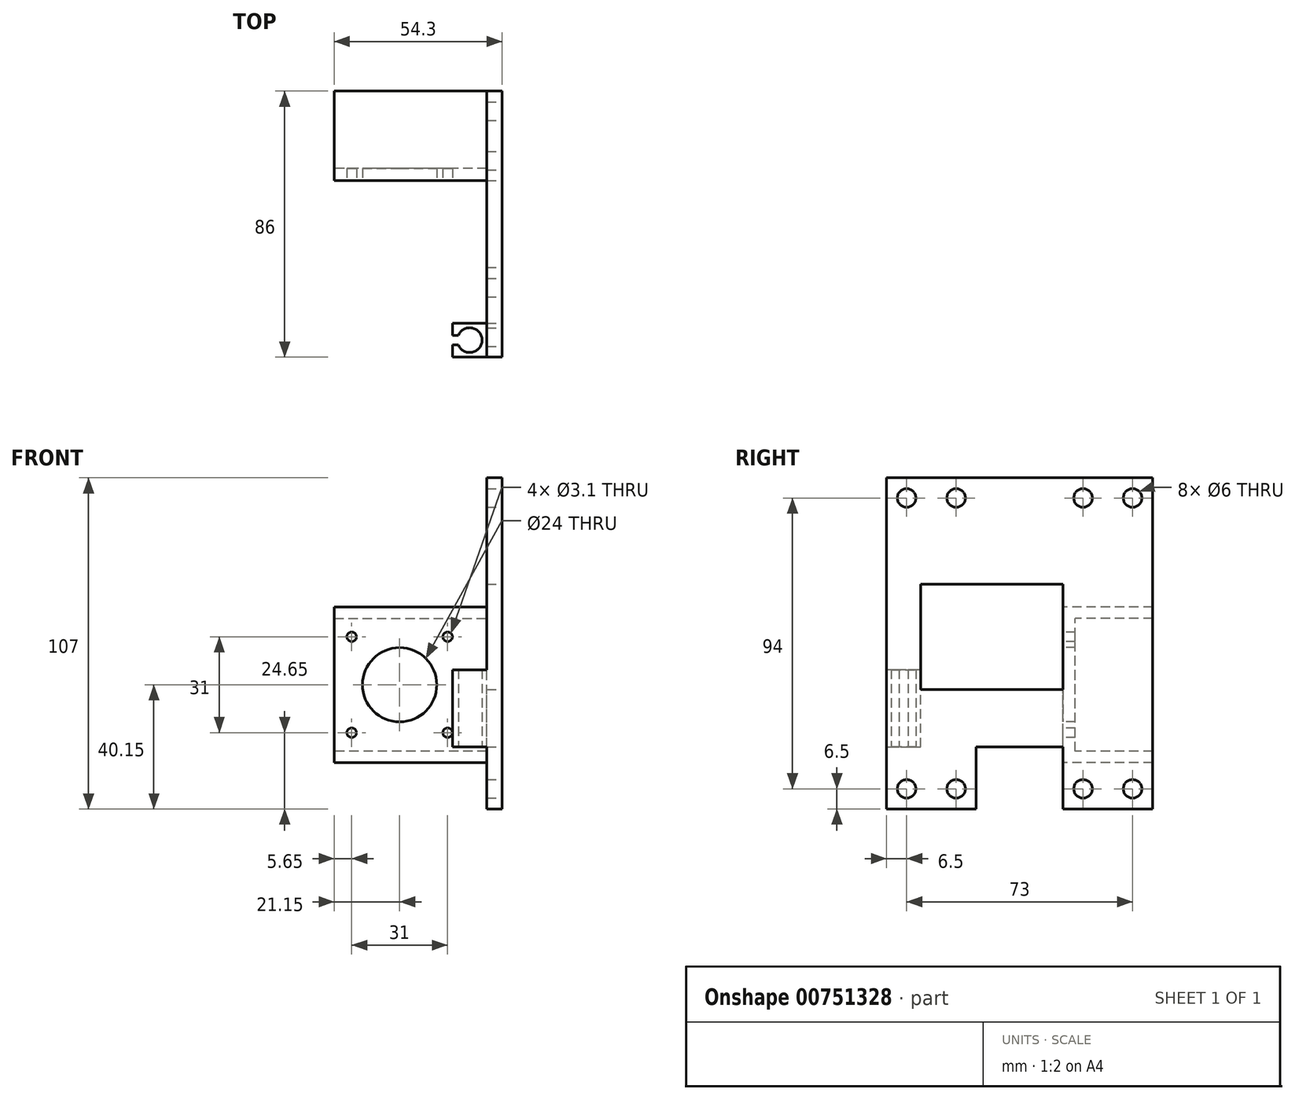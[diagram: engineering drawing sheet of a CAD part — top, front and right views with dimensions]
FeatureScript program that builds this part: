
annotation { "Feature Type Name" : "Feature", "Feature Type Description" : "" }
export const myFeature = defineFeature(function(context is Context, id is Id, definition is map)
    precondition{}
    {
        {
            var Q0;
            Q0=qCreatedBy(makeId("Front.planeOp"),FACE);
            var sketch = newSketch(context, id + "F0", { "sketchPlane" : qUnion([Q0])});
            skCircle(sketch, "E0", {"center": v(0, 0) * mm, "radius": 11 * mm, "construction": true});
            skLineSegment(sketch, "E1.bottom", {"start": v(15.5, 15.5) * mm, "end": v(-15.5, 15.5) * mm, "construction": true});
            skLineSegment(sketch, "E1.top", {"start": v(15.5, -15.5) * mm, "end": v(-15.5, -15.5) * mm, "construction": true});
            skLineSegment(sketch, "E1.left", {"start": v(15.5, 15.5) * mm, "end": v(15.5, -15.5) * mm, "construction": true});
            skLineSegment(sketch, "E1.right", {"start": v(-15.5, 15.5) * mm, "end": v(-15.5, -15.5) * mm, "construction": true});
            skCircle(sketch, "E2", {"center": v(15.5, 15.5) * mm, "radius": 1.5 * mm, "construction": true});
            skCircle(sketch, "E3", {"center": v(-15.5, 15.5) * mm, "radius": 1.5 * mm, "construction": true});
            skCircle(sketch, "E4", {"center": v(-15.5, -15.5) * mm, "radius": 1.5 * mm, "construction": true});
            skCircle(sketch, "E5", {"center": v(15.5, -15.5) * mm, "radius": 1.5 * mm, "construction": true});
            skCircle(sketch, "E6", {"center": v(15.5, 15.5) * mm, "radius": 17 * mm, "construction": true});
            skLineSegment(sketch, "E7.bottom", {"start": v(21.15, 21.15) * mm, "end": v(-21.15, 21.15) * mm, "construction": true});
            skLineSegment(sketch, "E7.top", {"start": v(21.15, -21.15) * mm, "end": v(-21.15, -21.15) * mm, "construction": true});
            skLineSegment(sketch, "E7.left", {"start": v(21.15, 21.15) * mm, "end": v(21.15, -21.15) * mm, "construction": true});
            skLineSegment(sketch, "E7.right", {"start": v(-21.15, 21.15) * mm, "end": v(-21.15, -21.15) * mm, "construction": true});
            skLineSegment(sketch, "E8", {"start": v(-43.83, -21) * mm, "end": v(88.96, -21) * mm, "construction": true});
            skSolve(sketch);
        }
        {
            var Q0;
            Q0=qCreatedBy(makeId("Top.planeOp"),FACE);
            var sketch = newSketch(context, id + "F1", { "sketchPlane" : qUnion([Q0])});
            skLineSegment(sketch, "E9.bottom", {"start": v(0, 0) * mm, "end": v(10.6, 0) * mm, "construction": true});
            skLineSegment(sketch, "E9.top", {"start": v(0, -13.5) * mm, "end": v(10.6, -13.5) * mm, "construction": true});
            skLineSegment(sketch, "E9.left", {"start": v(0, 0) * mm, "end": v(0, -13.5) * mm, "construction": true});
            skLineSegment(sketch, "E9.right", {"start": v(10.6, 0) * mm, "end": v(10.6, -13.5) * mm, "construction": true});
            skLineSegment(sketch, "E10", {"start": v(18.9, 0) * mm, "end": v(23.9, 0) * mm});
            skPoint(sketch, "E11", {"position": v(21.4, 0) * mm});
            skCircle(sketch, "E12", {"center": v(10.6, -13.5) * mm, "radius": 4 * mm, "construction": true});
            skLineSegment(sketch, "E13", {"start": v(10.6, -13.5) * mm, "end": v(10.6, -36.5) * mm, "construction": true});
            skLineSegment(sketch, "E14", {"start": v(10.6, -36.5) * mm, "end": v(19.6, -36.5) * mm, "construction": true});
            skCircle(sketch, "E15", {"center": v(19.6, -36.5) * mm, "radius": 4 * mm, "construction": true});
            skSolve(sketch);
        }
        {
            var Q0;
            Q0=qCreatedBy(makeId("Front.planeOp"),FACE);
            var sketch = newSketch(context, id + "F2", { "sketchPlane" : qUnion([Q0])});
            skLineSegment(sketch, "E16.0", {"start": v(33.15, 60.35) * mm, "end": v(33.15, -33.65) * mm});
            skLineSegment(sketch, "E17", {"start": v(33.15, 60.35) * mm, "end": v(33.15, 66.85) * mm});
            skLineSegment(sketch, "E18", {"start": v(33.15, -33.65) * mm, "end": v(33.15, -40.15) * mm});
            skLineSegment(sketch, "E19.0", {"start": v(29.15, -25.15) * mm, "end": v(-21.15, -25.15) * mm});
            skLineSegment(sketch, "E20", {"start": v(29.15, -25.15) * mm, "end": v(29.15, -40.15) * mm});
            skLineSegment(sketch, "E21", {"start": v(29.15, -40.15) * mm, "end": v(33.15, -40.15) * mm});
            skLineSegment(sketch, "E22.0", {"start": v(21.45, -21.45) * mm, "end": v(-21.15, -21.45) * mm});
            skLineSegment(sketch, "E22.1", {"start": v(21.45, 66.85) * mm, "end": v(21.45, -21.45) * mm, "construction": true});
            skLineSegment(sketch, "E23", {"start": v(-21.15, -21.45) * mm, "end": v(-21.15, -25.15) * mm});
            skLineSegment(sketch, "E24", {"start": v(21.45, 66.85) * mm, "end": v(33.15, 66.85) * mm});
            skPoint(sketch, "E25.0", {"position": v(-21.15, 21.15) * mm});
            skLineSegment(sketch, "E26", {"start": v(-21.15, 21.15) * mm, "end": v(21.45, 21.15) * mm, "construction": true});
            skLineSegment(sketch, "E27", {"start": v(-21.15, 21.15) * mm, "end": v(-21.15, -21.45) * mm});
            skCircle(sketch, "E28.0", {"center": v(0, 0) * mm, "radius": 12 * mm});
            skCircle(sketch, "E29.0", {"center": v(15.5, 15.5) * mm, "radius": 1.55 * mm});
            skCircle(sketch, "E30.0", {"center": v(-15.5, 15.5) * mm, "radius": 1.55 * mm});
            skCircle(sketch, "E31.0", {"center": v(-15.5, -15.5) * mm, "radius": 1.55 * mm});
            skCircle(sketch, "E32.0", {"center": v(15.5, -15.5) * mm, "radius": 1.55 * mm});
            skLineSegment(sketch, "E33", {"start": v(29.15, -21.45) * mm, "end": v(29.15, 66.85) * mm});
            skLineSegment(sketch, "E34", {"start": v(21.45, -21.45) * mm, "end": v(29.15, -21.45) * mm});
            skLineSegment(sketch, "E35", {"start": v(21.45, 21.15) * mm, "end": v(29.15, 21.15) * mm, "construction": true});
            skLineSegment(sketch, "E36", {"start": v(29.15, -21.45) * mm, "end": v(29.15, -25.15) * mm});
            skLineSegment(sketch, "E37.0", {"start": v(-21.15, 21.45) * mm, "end": v(29.15, 21.45) * mm});
            skLineSegment(sketch, "E38", {"start": v(-21.15, 21.15) * mm, "end": v(-21.15, 25.15) * mm});
            skLineSegment(sketch, "E39", {"start": v(-21.15, 25.15) * mm, "end": v(29.15, 25.15) * mm});
            skSolve(sketch);
        }
        {
            var Q0;
            Q0=qCreatedBy(makeId("Right.planeOp"),FACE);
            var sketch = newSketch(context, id + "F3", { "sketchPlane" : qUnion([Q0])});
            skPoint(sketch, "E40.0", {"position": v(0, 66.85) * mm});
            skPoint(sketch, "E41.0", {"position": v(0, -40.15) * mm});
            skPoint(sketch, "E42.0", {"position": v(0, 60.35) * mm});
            skPoint(sketch, "E43.0", {"position": v(0, -33.65) * mm});
            skLineSegment(sketch, "E44", {"start": v(0, 66.85) * mm, "end": v(29, 66.85) * mm});
            skLineSegment(sketch, "E45", {"start": v(29, 66.85) * mm, "end": v(29, -40.15) * mm});
            skLineSegment(sketch, "E46", {"start": v(29, -40.15) * mm, "end": v(0, -40.15) * mm});
            skLineSegment(sketch, "E47", {"start": v(0, 66.85) * mm, "end": v(-57, 66.85) * mm});
            skLineSegment(sketch, "E48", {"start": v(-57, 66.85) * mm, "end": v(-57, 40.85) * mm});
            skLineSegment(sketch, "E49", {"start": v(0, 0) * mm, "end": v(4, 0) * mm});
            skCircle(sketch, "E50", {"center": v(22.5, -33.65) * mm, "radius": 3 * mm});
            skCircle(sketch, "E51", {"center": v(6.5, -33.65) * mm, "radius": 3 * mm});
            skCircle(sketch, "E52", {"center": v(22.5, 60.35) * mm, "radius": 3 * mm});
            skCircle(sketch, "E53", {"center": v(6.5, 60.35) * mm, "radius": 3 * mm});
            skCircle(sketch, "E54", {"center": v(-34.5, 60.35) * mm, "radius": 3 * mm});
            skCircle(sketch, "E55", {"center": v(-50.5, 60.35) * mm, "radius": 3 * mm});
            skLineSegment(sketch, "E56", {"start": v(22.5, 60.35) * mm, "end": v(6.5, 60.35) * mm, "construction": true});
            skLineSegment(sketch, "E57", {"start": v(-34.5, 60.35) * mm, "end": v(-50.5, 60.35) * mm, "construction": true});
            skLineSegment(sketch, "E58", {"start": v(22.5, -33.65) * mm, "end": v(6.5, -33.65) * mm, "construction": true});
            skPoint(sketch, "E59", {"position": v(14.5, 60.35) * mm});
            skPoint(sketch, "E60", {"position": v(-42.5, 60.35) * mm});
            skLineSegment(sketch, "E61.0", {"start": v(-40.5, 0) * mm, "end": v(-32.5, 0) * mm, "construction": true});
            skLineSegment(sketch, "E62", {"start": v(-57, 40.85) * mm, "end": v(-57, -20.15) * mm});
            skLineSegment(sketch, "E63", {"start": v(-57, -20.15) * mm, "end": v(0, -20.15) * mm});
            skLineSegment(sketch, "E64", {"start": v(0, -20.15) * mm, "end": v(0, -40.15) * mm});
            skPoint(sketch, "E65.0", {"position": v(0, 15.5) * mm});
            skLineSegment(sketch, "E66.bottom", {"start": v(0, 32.5) * mm, "end": v(-46, 32.5) * mm});
            skLineSegment(sketch, "E66.top", {"start": v(0, -1.5) * mm, "end": v(-46, -1.5) * mm});
            skLineSegment(sketch, "E66.left", {"start": v(0, 32.5) * mm, "end": v(0, -1.5) * mm});
            skLineSegment(sketch, "E66.right", {"start": v(-46, 32.5) * mm, "end": v(-46, -1.5) * mm});
            skLineSegment(sketch, "E67", {"start": v(-46, -20.15) * mm, "end": v(-46, 4.85) * mm});
            skLineSegment(sketch, "E68", {"start": v(-46, 4.85) * mm, "end": v(-57, 4.85) * mm});
            skPoint(sketch, "E69.0", {"position": v(-13.5, 0) * mm});
            skLineSegment(sketch, "E70", {"start": v(-51.5, 4.85) * mm, "end": v(-51.5, -20.15) * mm, "construction": true});
            skPoint(sketch, "E71", {"position": v(14.5, -33.65) * mm});
            skLineSegment(sketch, "E72", {"start": v(-57, -20.15) * mm, "end": v(-57, -40.15) * mm});
            skLineSegment(sketch, "E73", {"start": v(-57, -40.15) * mm, "end": v(-28, -40.15) * mm});
            skLineSegment(sketch, "E74", {"start": v(-28, -40.15) * mm, "end": v(-28, -20.15) * mm});
            skCircle(sketch, "E75", {"center": v(-34.5, -33.65) * mm, "radius": 3 * mm});
            skCircle(sketch, "E76", {"center": v(-50.5, -33.65) * mm, "radius": 3 * mm});
            skLineSegment(sketch, "E77", {"start": v(-34.5, -33.65) * mm, "end": v(-50.5, -33.65) * mm, "construction": true});
            skPoint(sketch, "E78", {"position": v(-42.5, -33.65) * mm});
            skSolve(sketch);
        }
        {
            var Q0;
            Q0=makeQuery(id+"F2.imprint","IMPRINT",FACE,{"disambiguationData":[TD([[makeQuery(id+"F2.imprint","IMPRINT",EDGE,{"derivedFrom":sQuery(id+"F2.wireOp",EDGE,"E22.0")}),-1.0]])]});
            extrude(context, id + "F4", {"entities" : qUnion([Q0]), "oppositeDirection" : true, "depth" : 4 * mm, "offsetDistance" : 25 * mm});
        }
        {
            var Q0;
            Q0 = qSketchRegion(id + "F3", true);
            extrude(context, id + "F5", {"entities" : qUnion([Q0]), "oppositeDirection" : true, "depth" : 5 * mm, "offsetDistance" : 25 * mm});
        }
        {
            var Q0;
            {var subQ4=sQuery(id+"F3.wireOp",EDGE,"E67");Q0=makeQuery(id+"F3.imprint","IMPRINT",FACE,{"disambiguationData":[TD([[makeQuery(id+"F3.imprint","IMPRINT",EDGE,{"derivedFrom":subQ4}),1.0]])]});}
            extrude(context, id + "F6", {"entities" : qUnion([Q0]), "operationType" : NewBodyOperationType.ADD, "oppositeDirection" : true, "depth" : (5 + 11) * mm, "offsetDistance" : 25 * mm});
        }
        {
            var Q0;
            Q0=makeQuery(id+"F5.opExtrude","SWEPT_BODY",BODY,{"disambiguationData":[OSD([sQuery(id+"F3.wireOp",EDGE,"E44"),sQuery(id+"F3.wireOp",EDGE,"E45"),sQuery(id+"F3.wireOp",EDGE,"E46"),sQuery(id+"F3.wireOp",EDGE,"E47"),sQuery(id+"F3.wireOp",EDGE,"E48"),sQuery(id+"F3.wireOp",EDGE,"lw1fPIlm-i3EK-XiMf-CbQ2-mbzRzj0yqOiF"),sQuery(id+"F3.wireOp",EDGE,"4HJIKtKt-m902-pW4s-rPNS-Hvcr5oIB9F0y"),sQuery(id+"F3.wireOp",EDGE,"E50"),sQuery(id+"F3.wireOp",EDGE,"E51"),sQuery(id+"F3.wireOp",EDGE,"E52"),sQuery(id+"F3.wireOp",EDGE,"E53"),sQuery(id+"F3.wireOp",EDGE,"E54"),sQuery(id+"F3.wireOp",EDGE,"E55")])]});
            var Q1;
            Q1=sQuery(id+"F3.wireOp",VERTEX,"E42.0");
            var Q2;
            Q2=sQuery(id+"F2.wireOp",VERTEX,"E16.0.start");
            transform(context, id + "F7", {"entities" : qUnion([Q0]), "transformType" : TransformType.TRANSLATION_ENTITY, "oppositeDirectionEntity" : false, "transformLine" : qUnion([Q1, Q2]), "makeCopy" : false});
        }
        {
            var Q0;
            Q0=makeQuery(id+"F2.imprint","IMPRINT",FACE,{"disambiguationData":[TD([[makeQuery(id+"F2.imprint","IMPRINT",EDGE,{"derivedFrom":sQuery(id+"F2.wireOp",EDGE,"E19.0")}),-1.0]])]});
            var Q1;
            {var subQ0=sQuery(id+"F2.wireOp",EDGE,"E37.0");Q1=makeQuery(id+"F2.imprint","IMPRINT",FACE,{"disambiguationData":[TD([[makeQuery(id+"F2.imprint","IMPRINT",EDGE,{"derivedFrom":subQ0}),1.0]])]});}
            var Q2;
            Q2=makeQuery(id+"F5.opExtrude","SWEPT_FACE",FACE,{"disambiguationData":[OSD([sQuery(id+"F3.wireOp",EDGE,"E45")])]});
            extrude(context, id + "F8", {"entities" : qUnion([Q0, Q1]), "operationType" : NewBodyOperationType.ADD, "endBound" : BoundingType.UP_TO_SURFACE, "oppositeDirection" : true, "depth" : 25 * mm, "endBoundEntityFace" : qUnion([Q2]), "offsetDistance" : 25 * mm});
        }
        {
            var Q0;
            Q0=makeQuery(id+"F6.opExtrude","SWEPT_FACE",FACE,{"disambiguationData":[OSD([sQuery(id+"F3.wireOp",EDGE,"E63")])]});
            var sketch = newSketch(context, id + "F9", { "sketchPlane" : qUnion([Q0])});
            skArc(sketch, "E79", {"start": v(18.94, 50) * mm, "mid": v(26.65, 51.5) * mm, "end": v(18.94, 53) * mm});
            skPoint(sketch, "E79.centerSnap0", {"position": v(17.15, 51.5) * mm});
            skPoint(sketch, "E79.centerSnap1", {"position": v(22.65, 57) * mm});
            skLineSegment(sketch, "E80", {"start": v(18.94, 53) * mm, "end": v(9.17, 53) * mm});
            skLineSegment(sketch, "E81", {"start": v(18.94, 50) * mm, "end": v(9.17, 50) * mm});
            skLineSegment(sketch, "E82", {"start": v(9.17, 53) * mm, "end": v(9.17, 50) * mm});
            skLineSegment(sketch, "E83", {"start": v(17.15, 51.5) * mm, "end": v(9.17, 51.5) * mm, "construction": true});
            skPoint(sketch, "E84", {"position": v(9.17, 51.5) * mm});
            skSolve(sketch);
        }
        {
            var Q0;
            Q0 = qSketchRegion(id + "F9", true);
            var Q1;
            Q1=makeQuery(id+"F6.opExtrude","SWEPT_FACE",FACE,{"disambiguationData":[OSD([sQuery(id+"F3.wireOp",EDGE,"E68")])]});
            extrude(context, id + "F10", {"entities" : qUnion([Q0]), "operationType" : NewBodyOperationType.REMOVE, "endBound" : BoundingType.UP_TO_SURFACE, "oppositeDirection" : true, "depth" : 25 * mm, "endBoundEntityFace" : qUnion([Q1]), "offsetDistance" : 25 * mm});
        }
    });
